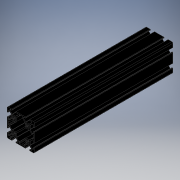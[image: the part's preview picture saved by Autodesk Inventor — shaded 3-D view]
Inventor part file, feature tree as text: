
AUTODESK INVENTOR PART (.ipt)
format: ipt  version: 2019 (Build 230136000, 136)  size: 481,792 bytes
history: native  units: mm
features: extrude x1, sketch x1
ambient origin geometry x8: Origin, YZ Plane, XZ Plane, XY Plane, X Axis, Y Axis, Z Axis, Center Point
bodies: Solid1 (feature_tree)
feature tree (2):
  extrude  "Extrusion1"  [1 undecoded]
  sketch  "Sketch_1"  dims[d0=203.2mm d1=0.0mm]
note: 1 required parameter value undecoded (feature->parameter linkage not recoverable at this tier; creation-order binding heuristic only, values carry confidence <= 0.55)
